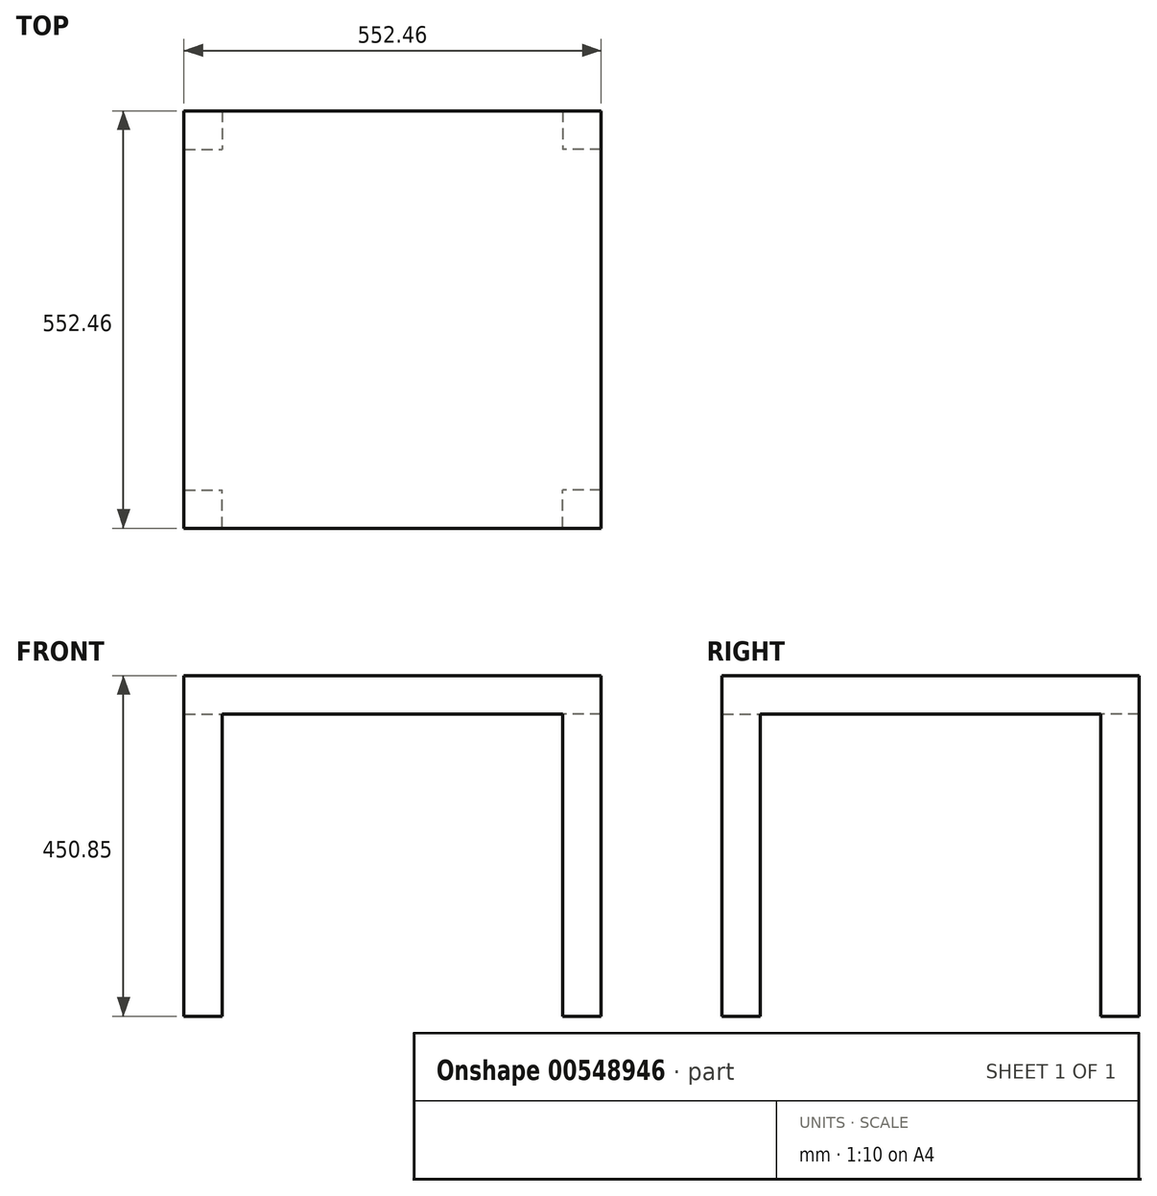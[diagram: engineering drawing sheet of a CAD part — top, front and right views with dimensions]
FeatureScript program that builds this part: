
annotation { "Feature Type Name" : "Feature", "Feature Type Description" : "" }
export const myFeature = defineFeature(function(context is Context, id is Id, definition is map)
    precondition{}
    {
        {
            var Q0;
            Q0=qCreatedBy(makeId("Top.planeOp"),FACE);
            var sketch = newSketch(context, id + "F0", { "sketchPlane" : qUnion([Q0])});
            skLineSegment(sketch, "E0.bottom", {"start": v(-276.23, 276.23) * mm, "end": v(276.23, 276.23) * mm});
            skLineSegment(sketch, "E0.top", {"start": v(-276.23, -276.23) * mm, "end": v(276.23, -276.23) * mm});
            skLineSegment(sketch, "E0.left", {"start": v(-276.23, 276.23) * mm, "end": v(-276.23, -276.23) * mm});
            skLineSegment(sketch, "E0.right", {"start": v(276.23, 276.23) * mm, "end": v(276.23, -276.23) * mm});
            skPoint(sketch, "E0.middle", {"position": v(0, 0) * mm});
            skSolve(sketch);
        }
        {
            var Q0;
            Q0=makeQuery(id+"F0.imprint","IMPRINT",FACE,{"disambiguationData":[TD([[makeQuery(id+"F0.imprint","IMPRINT",EDGE,{"derivedFrom":sQuery(id+"F0.wireOp",EDGE,"E0.bottom")}),-1.0]])]});
            extrude(context, id + "F1", {"entities" : qUnion([Q0]), "depth" : 50.8 * mm, "offsetDistance" : 25.4 * mm});
        }
        {
            var Q0;
            Q0=makeQuery(id+"F1.opExtrude","CAP_FACE",FACE,{"disambiguationData":[OSD([sQuery(id+"F0.wireOp",EDGE,"E0.bottom"),sQuery(id+"F0.wireOp",EDGE,"E0.top"),sQuery(id+"F0.wireOp",EDGE,"E0.left"),sQuery(id+"F0.wireOp",EDGE,"E0.right")])],"isStart":true});
            var sketch = newSketch(context, id + "F2", { "sketchPlane" : qUnion([Q0])});
            skLineSegment(sketch, "E1.bottom", {"start": v(-276.23, 276.23) * mm, "end": v(-225.43, 276.23) * mm});
            skLineSegment(sketch, "E1.top", {"start": v(-276.23, 225.43) * mm, "end": v(-225.43, 225.43) * mm});
            skLineSegment(sketch, "E1.left", {"start": v(-276.23, 276.23) * mm, "end": v(-276.23, 225.43) * mm});
            skLineSegment(sketch, "E1.right", {"start": v(-225.43, 276.23) * mm, "end": v(-225.43, 225.43) * mm});
            skLineSegment(sketch, "E2.bottom", {"start": v(276.23, 276.23) * mm, "end": v(225.43, 276.23) * mm});
            skLineSegment(sketch, "E2.top", {"start": v(276.23, 225.43) * mm, "end": v(225.43, 225.43) * mm});
            skLineSegment(sketch, "E2.left", {"start": v(276.23, 276.23) * mm, "end": v(276.23, 225.43) * mm});
            skLineSegment(sketch, "E2.right", {"start": v(225.43, 276.23) * mm, "end": v(225.43, 225.43) * mm});
            skLineSegment(sketch, "E3.bottom", {"start": v(-276.23, -276.23) * mm, "end": v(-225.43, -276.23) * mm});
            skLineSegment(sketch, "E3.top", {"start": v(-276.23, -225.43) * mm, "end": v(-225.43, -225.43) * mm});
            skLineSegment(sketch, "E3.left", {"start": v(-276.23, -276.23) * mm, "end": v(-276.23, -225.43) * mm});
            skLineSegment(sketch, "E3.right", {"start": v(-225.43, -276.23) * mm, "end": v(-225.43, -225.43) * mm});
            skLineSegment(sketch, "E4.bottom", {"start": v(276.23, -276.23) * mm, "end": v(225.43, -276.23) * mm});
            skLineSegment(sketch, "E4.top", {"start": v(276.23, -225.43) * mm, "end": v(225.43, -225.43) * mm});
            skLineSegment(sketch, "E4.left", {"start": v(276.23, -276.23) * mm, "end": v(276.23, -225.43) * mm});
            skLineSegment(sketch, "E4.right", {"start": v(225.43, -276.23) * mm, "end": v(225.43, -225.43) * mm});
            skSolve(sketch);
        }
        {
            var Q0;
            Q0 = qSketchRegion(id + "F2", true);
            extrude(context, id + "F3", {"entities" : qUnion([Q0]), "operationType" : NewBodyOperationType.ADD, "depth" : 400.05 * mm, "offsetDistance" : 25.4 * mm});
        }
    });
